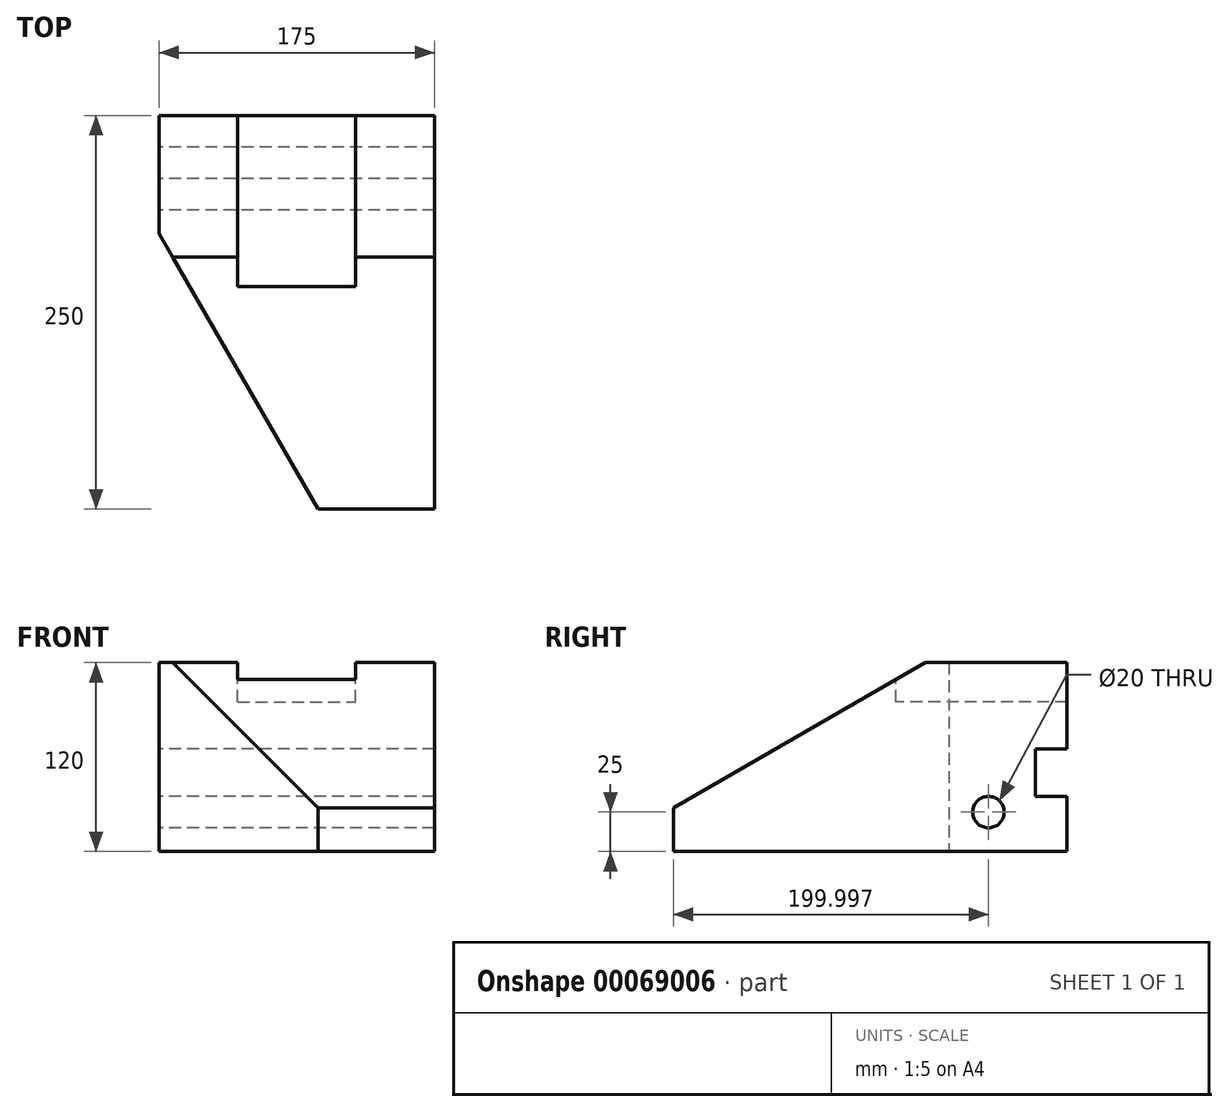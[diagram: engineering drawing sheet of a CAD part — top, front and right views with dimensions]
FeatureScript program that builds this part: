
annotation { "Feature Type Name" : "Feature", "Feature Type Description" : "" }
export const myFeature = defineFeature(function(context is Context, id is Id, definition is map)
    precondition{}
    {
        {
            var Q0;
            Q0=qCreatedBy(makeId("Top.planeOp"),FACE);
            var sketch = newSketch(context, id + "F0", { "sketchPlane" : qUnion([Q0])});
            skLineSegment(sketch, "E0.bottom", {"start": v(-79.9, 96.08) * mm, "end": v(95.1, 96.08) * mm});
            skLineSegment(sketch, "E0.top", {"start": v(-79.9, -153.92) * mm, "end": v(95.1, -153.92) * mm});
            skLineSegment(sketch, "E0.left", {"start": v(-79.9, 96.08) * mm, "end": v(-79.9, -153.92) * mm});
            skLineSegment(sketch, "E0.right", {"start": v(95.1, 96.08) * mm, "end": v(95.1, -153.92) * mm});
            skPoint(sketch, "E1", {"position": v(-79.9, 21.08) * mm});
            skLineSegment(sketch, "E2", {"start": v(-79.9, 21.08) * mm, "end": v(21.13, -153.92) * mm});
            skPoint(sketch, "E3", {"position": v(-29.9, 96.08) * mm});
            skLineSegment(sketch, "E4.bottom", {"start": v(-29.9, 96.08) * mm, "end": v(32.76, 96.08) * mm});
            skLineSegment(sketch, "E4.right", {"start": v(32.76, 96.08) * mm, "end": v(32.76, -65.32) * mm});
            skSolve(sketch);
        }
        {
            var Q0;
            {var subQ4=sQuery(id+"F0.wireOp",EDGE,"E0.right");Q0=makeQuery(id+"F0.imprint","IMPRINT",FACE,{"disambiguationData":[TD([[makeQuery(id+"F0.imprint","IMPRINT",EDGE,{"derivedFrom":subQ4}),-1.0]])]});}
            extrude(context, id + "F1", {"entities" : qUnion([Q0]), "depth" : 120 * mm});
        }
        {
            var Q0;
            Q0=makeQuery(id+"F1.opExtrude","SWEPT_FACE",FACE,{"disambiguationData":[OSD([sQuery(id+"F0.wireOp",EDGE,"E0.right")])]});
            var sketch = newSketch(context, id + "F2", { "sketchPlane" : qUnion([Q0])});
            skPoint(sketch, "E5", {"position": v(6.08, 120) * mm});
            skLineSegment(sketch, "E6", {"start": v(6.08, 120) * mm, "end": v(-153.92, 27.62) * mm});
            skSolve(sketch);
        }
        {
            var Q0;
            Q0 = qSketchRegion(id + "F2", true);
            var Q1;
            {var subQ0=sQuery(id+"F2.wireOp",EDGE,"E6");Q1=makeQuery(id+"F2.imprint","IMPRINT",FACE,{"disambiguationData":[TD([[makeQuery(id+"F2.imprint","IMPRINT",EDGE,{"derivedFrom":subQ0}),-1.0]])]});}
            extrude(context, id + "F3", {"entities" : qUnion([Q0, Q1]), "operationType" : NewBodyOperationType.REMOVE, "endBound" : BoundingType.THROUGH_ALL, "oppositeDirection" : true, "depth" : 77 * mm});
        }
        {
            var Q0;
            Q0=makeQuery(id+"F1.opExtrude","CAP_FACE",FACE,{"disambiguationData":[OSD([sQuery(id+"F0.wireOp",EDGE,"E0.bottom"),sQuery(id+"F0.wireOp",EDGE,"E0.top"),sQuery(id+"F0.wireOp",EDGE,"E0.left"),sQuery(id+"F0.wireOp",EDGE,"E0.right"),sQuery(id+"F0.wireOp",EDGE,"E2"),sQuery(id+"F0.wireOp",EDGE,"E4.bottom")])],"isStart":false});
            var sketch = newSketch(context, id + "F4", { "sketchPlane" : qUnion([Q0])});
            skPoint(sketch, "E7", {"position": v(-29.9, 96.08) * mm});
            skLineSegment(sketch, "E8.bottom", {"start": v(-29.9, 96.08) * mm, "end": v(45.1, 96.08) * mm});
            skLineSegment(sketch, "E8.top", {"start": v(-29.9, -12.73) * mm, "end": v(45.1, -12.73) * mm});
            skLineSegment(sketch, "E8.left", {"start": v(-29.9, 96.08) * mm, "end": v(-29.9, -12.73) * mm});
            skLineSegment(sketch, "E8.right", {"start": v(45.1, 96.08) * mm, "end": v(45.1, -12.73) * mm});
            skSolve(sketch);
        }
        {
            var Q0;
            Q0 = qSketchRegion(id + "F4", true);
            extrude(context, id + "F5", {"entities" : qUnion([Q0]), "operationType" : NewBodyOperationType.REMOVE, "oppositeDirection" : true, "depth" : 25 * mm});
        }
        {
            var Q0;
            Q0=makeQuery(id+"F1.opExtrude","SWEPT_FACE",FACE,{"disambiguationData":[OSD([sQuery(id+"F0.wireOp",EDGE,"E0.left")])]});
            var sketch = newSketch(context, id + "F6", { "sketchPlane" : qUnion([Q0])});
            skPoint(sketch, "E9", {"position": v(-96.08, 35) * mm});
            skPoint(sketch, "E10", {"position": v(-76.08, 35) * mm});
            skLineSegment(sketch, "E11.bottom", {"start": v(-96.08, 35) * mm, "end": v(-76.08, 35) * mm});
            skLineSegment(sketch, "E11.top", {"start": v(-96.08, 65) * mm, "end": v(-76.08, 65) * mm});
            skLineSegment(sketch, "E11.left", {"start": v(-96.08, 35) * mm, "end": v(-96.08, 65) * mm});
            skLineSegment(sketch, "E11.right", {"start": v(-76.08, 35) * mm, "end": v(-76.08, 65) * mm});
            skPoint(sketch, "E12", {"position": v(-46.08, 0) * mm});
            skPoint(sketch, "E13", {"position": v(-46.08, 25) * mm});
            skCircle(sketch, "E14", {"center": v(-46.08, 25) * mm, "radius": 10 * mm});
            skSolve(sketch);
        }
        {
            var Q0;
            Q0 = qSketchRegion(id + "F6", true);
            extrude(context, id + "F7", {"entities" : qUnion([Q0]), "operationType" : NewBodyOperationType.REMOVE, "endBound" : BoundingType.THROUGH_ALL, "oppositeDirection" : true, "depth" : 25 * mm});
        }
    });
